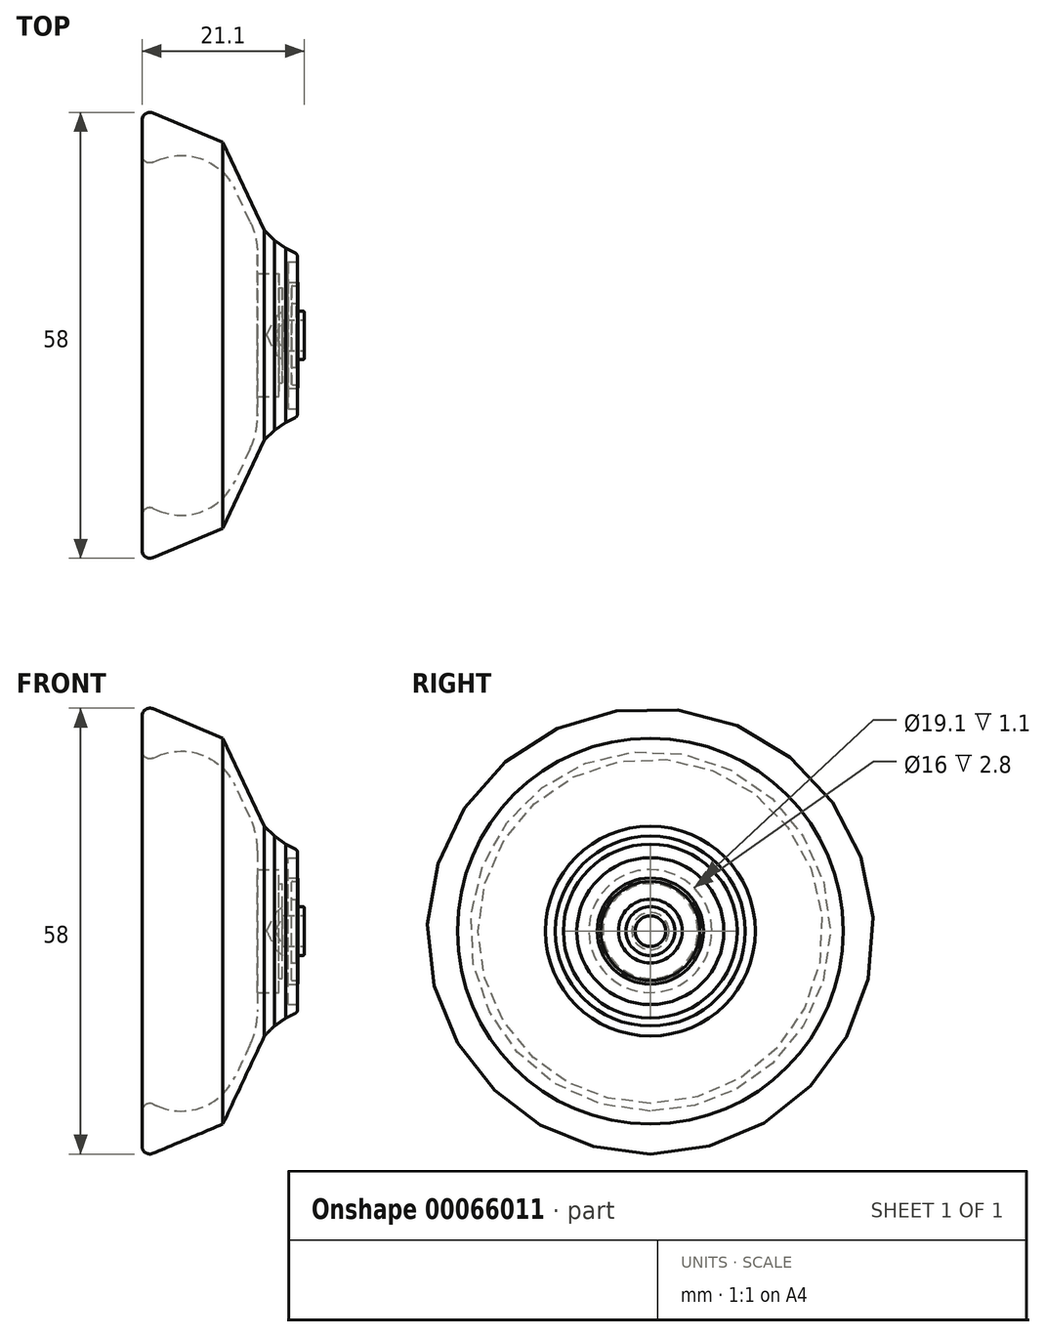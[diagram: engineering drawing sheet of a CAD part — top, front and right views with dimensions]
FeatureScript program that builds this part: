
annotation { "Feature Type Name" : "Feature", "Feature Type Description" : "" }
export const myFeature = defineFeature(function(context is Context, id is Id, definition is map)
    precondition{}
    {
        {
            var Q0;
            Q0=qCreatedBy(makeId("Front.planeOp"),FACE);
            var sketch = newSketch(context, id + "F0", { "sketchPlane" : qUnion([Q0])});
            skLineSegment(sketch, "E0", {"start": v(-1.4, 2) * mm, "end": v(-4.2, 2) * mm});
            skLineSegment(sketch, "E1", {"start": v(-4.2, 2) * mm, "end": v(-5.19, 0) * mm});
            skLineSegment(sketch, "E2", {"start": v(-5.19, 0) * mm, "end": v(-6.3, 0) * mm});
            skLineSegment(sketch, "E3", {"start": v(-7.5, 12.74) * mm, "end": v(-10.45, 19) * mm});
            skLineSegment(sketch, "E4", {"start": v(-22.5, 23.42) * mm, "end": v(-22.5, 29.5) * mm});
            skLineSegment(sketch, "E5", {"start": v(-1.4, 3.17) * mm, "end": v(-2.4, 3.17) * mm});
            skLineSegment(sketch, "E6", {"start": v(-2.4, 3.17) * mm, "end": v(-2.4, 4.15) * mm});
            skLineSegment(sketch, "E7", {"start": v(-2.4, 4.15) * mm, "end": v(-3.05, 4.15) * mm});
            skLineSegment(sketch, "E8", {"start": v(-3.05, 4.15) * mm, "end": v(-3.05, 6.45) * mm});
            skLineSegment(sketch, "E9", {"start": v(-3.05, 6.45) * mm, "end": v(-2.25, 6.45) * mm});
            skLineSegment(sketch, "E10", {"start": v(-2.25, 6.45) * mm, "end": v(-2.25, 6.9) * mm});
            skLineSegment(sketch, "E11", {"start": v(-2.25, 6.9) * mm, "end": v(-3.5, 6.9) * mm});
            skLineSegment(sketch, "E12", {"start": v(-3.5, 6.9) * mm, "end": v(-3.5, 9.55) * mm});
            skLineSegment(sketch, "E13", {"start": v(-3.5, 9.55) * mm, "end": v(-2.3, 9.55) * mm});
            skLineSegment(sketch, "E14", {"start": v(-2.3, 9.55) * mm, "end": v(-2.3, 10.55) * mm});
            skLineSegment(sketch, "E15", {"start": v(-1.4, 3.17) * mm, "end": v(-1.4, 2) * mm});
            skLineSegment(sketch, "E16", {"start": v(-2.3, 10.55) * mm, "end": v(-2.3, 10.55) * mm});
            skLineSegment(sketch, "E17", {"start": v(-21.1, 22.5) * mm, "end": v(-20.5, 22.76) * mm});
            skPoint(sketch, "E18.visualSharp", {"position": v(-13.64, 25.78) * mm});
            skArc(sketch, "E18.filletArc", {"start": v(-10.45, 19) * mm, "mid": v(-14.71, 22.92) * mm, "end": v(-20.5, 22.76) * mm});
            skPoint(sketch, "E19.visualSharp", {"position": v(-22.5, 21.88) * mm});
            skArc(sketch, "E19.filletArc", {"start": v(-22.5, 23.42) * mm, "mid": v(-22.05, 22.58) * mm, "end": v(-21.1, 22.5) * mm});
            skLineSegment(sketch, "E20", {"start": v(-2.3, 10.55) * mm, "end": v(-3.82, 11.31) * mm});
            skLineSegment(sketch, "E21", {"start": v(-3.82, 11.31) * mm, "end": v(-5.3, 12.35) * mm});
            skLineSegment(sketch, "E22", {"start": v(-5.3, 12.35) * mm, "end": v(-6.6, 13.65) * mm});
            skLineSegment(sketch, "E23", {"start": v(-6.6, 13.65) * mm, "end": v(-12, 25.1) * mm});
            skLineSegment(sketch, "E24", {"start": v(-22.5, 29.5) * mm, "end": v(-12, 25.1) * mm});
            skLineSegment(sketch, "E25", {"start": v(-7.5, 12.74) * mm, "end": v(-7.5, 8) * mm});
            skLineSegment(sketch, "E26", {"start": v(-7.5, 8) * mm, "end": v(-4.7, 8) * mm});
            skLineSegment(sketch, "E27", {"start": v(-4.7, 8) * mm, "end": v(-4.7, 6.17) * mm});
            skLineSegment(sketch, "E28", {"start": v(-4.7, 6.17) * mm, "end": v(-4.25, 6.17) * mm});
            skLineSegment(sketch, "E29", {"start": v(-4.25, 6.17) * mm, "end": v(-4.25, 3.17) * mm});
            skLineSegment(sketch, "E30", {"start": v(-6.3, 0) * mm, "end": v(-5.1, 2.42) * mm});
            skLineSegment(sketch, "E31", {"start": v(-5.1, 2.42) * mm, "end": v(-4.25, 3.17) * mm});
            skSolve(sketch);
        }
        {
            var Q0;
            Q0 = qSketchRegion(id + "F0", true);
            var Q1;
            Q1=sQuery(id+"F0.wireOp",EDGE,"E2");
            revolve(context, id + "F1", {"entities" : qUnion([Q0]), "axis" : qUnion([Q1]), "revolveType" : RevolveType.FULL});
        }
        {
            var Q0;
            Q0=makeQuery(id+"F1.opRevolve","SWEPT_EDGE",EDGE,{"disambiguationData":[OSD([sQuery(id+"F0.wireOp",EDGE,"E6"),sQuery(id+"F0.wireOp",EDGE,"E7")])]});
            var Q1;
            Q1=makeQuery(id+"F1.opRevolve","SWEPT_EDGE",EDGE,{"disambiguationData":[OSD([sQuery(id+"F0.wireOp",EDGE,"E7"),sQuery(id+"F0.wireOp",EDGE,"E8")])]});
            var Q2;
            Q2=makeQuery(id+"F1.opRevolve","SWEPT_EDGE",EDGE,{"disambiguationData":[OSD([sQuery(id+"F0.wireOp",EDGE,"E9"),sQuery(id+"F0.wireOp",EDGE,"E10")])]});
            var Q3;
            Q3=makeQuery(id+"F1.opRevolve","SWEPT_EDGE",EDGE,{"disambiguationData":[OSD([sQuery(id+"F0.wireOp",EDGE,"E10"),sQuery(id+"F0.wireOp",EDGE,"E11")])]});
            var Q4;
            Q4=makeQuery(id+"F1.opRevolve","SWEPT_EDGE",EDGE,{"disambiguationData":[OSD([sQuery(id+"F0.wireOp",EDGE,"E13"),sQuery(id+"F0.wireOp",EDGE,"E14")])]});
            var Q5;
            Q5=makeQuery(id+"F1.opRevolve","SWEPT_EDGE",EDGE,{"disambiguationData":[OSD([sQuery(id+"F0.wireOp",EDGE,"E8"),sQuery(id+"F0.wireOp",EDGE,"E9")])]});
            var Q6;
            Q6=makeQuery(id+"F1.opRevolve","SWEPT_EDGE",EDGE,{"disambiguationData":[OSD([sQuery(id+"F0.wireOp",EDGE,"E5"),sQuery(id+"F0.wireOp",EDGE,"E6")])]});
            fillet(context, id + "F2", {"entities" : qUnion([Q0, Q1, Q2, Q3, Q4, Q5, Q6]), "radius" : 0.1 * mm, "tangentPropagation" : true, "allowEdgeOverflow" : false});
        }
        {
            var Q0;
            Q0=makeQuery(id+"F1.opRevolve","SWEPT_EDGE",EDGE,{"disambiguationData":[OSD([sQuery(id+"F0.wireOp",EDGE,"E5"),sQuery(id+"F0.wireOp",EDGE,"E15")])]});
            fillet(context, id + "F3", {"entities" : qUnion([Q0]), "radius" : 0.2 * mm, "tangentPropagation" : true, "allowEdgeOverflow" : false});
        }
        {
            var Q0;
            Q0=makeQuery(id+"F1.opRevolve","SWEPT_EDGE",EDGE,{"disambiguationData":[OSD([sQuery(id+"F0.wireOp",EDGE,"E4"),sQuery(id+"F0.wireOp",EDGE,"qcfS0AuZ-xKJO-e0qy-MTLN-h3hrmbb2rTTs")])]});
            fillet(context, id + "F4", {"entities" : qUnion([Q0]), "radius" : 1 * mm, "tangentPropagation" : true, "allowEdgeOverflow" : false});
        }
        {
            var Q0;
            Q0=makeQuery(id+"F1.opRevolve","SWEPT_EDGE",EDGE,{"disambiguationData":[OSD([sQuery(id+"F0.wireOp",EDGE,"E3"),sQuery(id+"F0.wireOp",EDGE,"E25")])]});
            fillet(context, id + "F5", {"entities" : qUnion([Q0]), "radius" : 10 * mm, "tangentPropagation" : true, "allowEdgeOverflow" : false});
        }
        {
            var Q0;
            Q0=makeQuery(id+"F1.opRevolve","SWEPT_EDGE",EDGE,{"disambiguationData":[OSD([sQuery(id+"F0.wireOp",EDGE,"E14"),sQuery(id+"F0.wireOp",EDGE,"E20")])]});
            fillet(context, id + "F6", {"entities" : qUnion([Q0]), "radius" : 0.5 * mm, "tangentPropagation" : true, "allowEdgeOverflow" : false});
        }
    });
